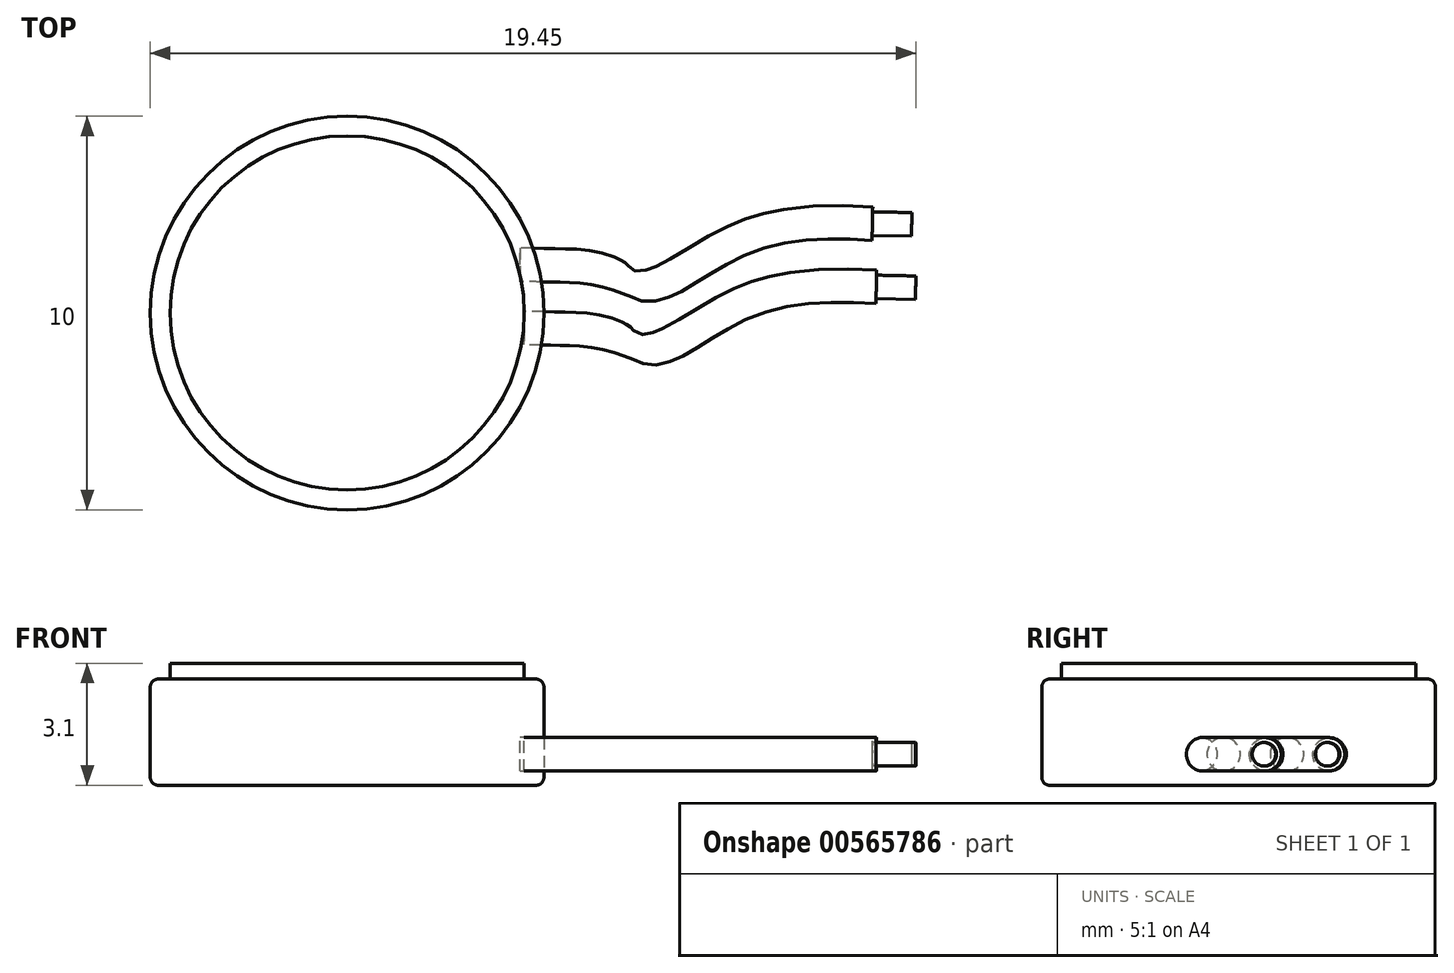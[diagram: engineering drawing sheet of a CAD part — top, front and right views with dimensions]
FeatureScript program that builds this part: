
annotation { "Feature Type Name" : "Feature", "Feature Type Description" : "" }
export const myFeature = defineFeature(function(context is Context, id is Id, definition is map)
    precondition{}
    {
        {
            var Q0;
            Q0=qCreatedBy(makeId("Top.planeOp"),FACE);
            var sketch = newSketch(context, id + "F0", { "sketchPlane" : qUnion([Q0])});
            skCircle(sketch, "E0", {"center": v(0, 0) * mm, "radius": 5 * mm});
            skSolve(sketch);
        }
        {
            var Q0;
            Q0=makeQuery(id+"F0.imprint","IMPRINT",FACE,{"disambiguationData":[TD([[makeQuery(id+"F0.imprint","IMPRINT",EDGE,{"derivedFrom":sQuery(id+"F0.wireOp",EDGE,"E0")}),1.0]])]});
            var Q1;
            Q1=sQuery(id+"F0.wireOp",EDGE,"E0");
            extrude(context, id + "F1", {"entities" : qUnion([Q0]), "surfaceEntities" : qUnion([Q1]), "depth" : 2.7 * mm, "offsetDistance" : 25 * mm});
        }
        {
            var Q0;
            Q0=makeQuery(id+"F1.opExtrude","CAP_FACE",FACE,{"disambiguationData":[OSD([sQuery(id+"F0.wireOp",EDGE,"E0")])],"isStart":false});
            var Q1;
            Q1=makeQuery(id+"F1.opExtrude","SWEPT_FACE",FACE,{"disambiguationData":[OSD([sQuery(id+"F0.wireOp",EDGE,"E0")])]});
            var Q2;
            Q2=makeQuery(id+"F1.opExtrude","CAP_FACE",FACE,{"disambiguationData":[OSD([sQuery(id+"F0.wireOp",EDGE,"E0")])],"isStart":true});
            fillet(context, id + "F2", {"entities" : qUnion([Q0, Q1, Q2]), "radius" : 0.2 * mm, "tangentPropagation" : true, "allowEdgeOverflow" : false});
        }
        {
            var Q0;
            Q0=makeQuery(id+"F1.opExtrude","CAP_FACE",FACE,{"disambiguationData":[OSD([sQuery(id+"F0.wireOp",EDGE,"E0")])],"isStart":false});
            var sketch = newSketch(context, id + "F3", { "sketchPlane" : qUnion([Q0])});
            skCircle(sketch, "E1", {"center": v(0, 0) * mm, "radius": 4.5 * mm});
            skSolve(sketch);
        }
        {
            var Q0;
            Q0=qCreatedBy(makeId("Right.planeOp"),FACE);
            var sketch = newSketch(context, id + "F4", { "sketchPlane" : qUnion([Q0])});
            skCircle(sketch, "E2", {"center": v(-5.9, -1.01) * mm, "radius": 0.53 * mm});
            skCircle(sketch, "E3.0", {"center": v(-5.9, -1.01) * mm, "radius": 0.43 * mm});
            skSolve(sketch);
        }
        {
            var Q0;
            Q0=qCreatedBy(makeId("Top.planeOp"),FACE);
            var sketch = newSketch(context, id + "F5", { "sketchPlane" : qUnion([Q0])});
            skFitSpline(sketch, "E4", {"points": [v(0.86, -7.42) * mm, v(2.15, -7.53) * mm, v(4.15, -7.61) * mm, v(6.53, -6.55) * mm, v(9.78, -6.4) * mm], "startDerivative": vector(6.34, -0.31) * mm, "endDerivative": vector(11.3, -0.8) * mm});
            skSolve(sketch);
        }
        {
            var Q0;
            Q0=makeQuery(id+"F4.imprint","IMPRINT",FACE,{"disambiguationData":[TD([[makeQuery(id+"F4.imprint","IMPRINT",EDGE,{"derivedFrom":sQuery(id+"F4.wireOp",EDGE,"E3.0")}),1.0]])]});
            var Q1;
            Q1=sQuery(id+"F5.wireOp",EDGE,"E4");
            sweep(context, id + "F6", {"profiles" : qUnion([Q0]), "path" : qUnion([Q1])});
        }
        {
            var Q0;
            Q0=makeQuery(id+"F6.opSweep","SWEPT_BODY",BODY,{"disambiguationData":[OSD([sQuery(id+"F4.wireOp",EDGE,"E3.0"),sQuery(id+"F5.wireOp",EDGE,"E4")])]});
            transform(context, id + "F7", {"entities" : qUnion([Q0]), "transformType" : TransformType.TRANSLATION_3D, "dx" : 5 * mm, "dy" : 6.12 * mm, "dz" : 1.6 * mm, "makeCopy" : false});
        }
        {
            var Q0;
            Q0=makeQuery(id+"F6.opSweep","SWEPT_BODY",BODY,{"disambiguationData":[OSD([sQuery(id+"F4.wireOp",EDGE,"E3.0"),sQuery(id+"F5.wireOp",EDGE,"E4")])]});
            transform(context, id + "F8", {"entities" : qUnion([Q0]), "transformType" : TransformType.TRANSLATION_3D, "dx" : 0 * mm, "dy" : 0 * mm, "dz" : 0.2 * mm, "makeCopy" : false});
        }
        {
            var Q0;
            Q0=makeQuery(id+"F6.opSweep","SWEPT_BODY",BODY,{"disambiguationData":[OSD([sQuery(id+"F4.wireOp",EDGE,"E3.0"),sQuery(id+"F5.wireOp",EDGE,"E4")])]});
            transform(context, id + "F9", {"entities" : qUnion([Q0]), "transformType" : TransformType.TRANSLATION_3D, "dx" : 0 * mm, "dy" : 1.3 * mm, "dz" : 0 * mm, "makeCopy" : true});
        }
        {
            var Q0;
            Q0=makeQuery(id+"F6.opSweep","SWEPT_BODY",BODY,{"disambiguationData":[OSD([sQuery(id+"F4.wireOp",EDGE,"E3.0"),sQuery(id+"F5.wireOp",EDGE,"E4")])]});
            transform(context, id + "F10", {"entities" : qUnion([Q0]), "transformType" : TransformType.TRANSLATION_3D, "dx" : -0.5 * mm, "dy" : -0.6 * mm, "dz" : 0 * mm, "makeCopy" : false});
        }
        {
            var Q0;
            Q0=makeQuery(id+"F9.opPattern","COPY",BODY,{"derivedFrom":makeQuery(id+"F6.opSweep","SWEPT_BODY",BODY,{"disambiguationData":[OSD([sQuery(id+"F4.wireOp",EDGE,"E3.0"),sQuery(id+"F5.wireOp",EDGE,"E4")])]}),"instanceName":"1"});
            transform(context, id + "F11", {"entities" : qUnion([Q0]), "transformType" : TransformType.TRANSLATION_3D, "dx" : -0.6 * mm, "dy" : -0.3 * mm, "dz" : 0 * mm, "makeCopy" : false});
        }
        {
            var Q0;
            Q0=makeQuery(id+"F3.imprint","IMPRINT",FACE,{"disambiguationData":[TD([[makeQuery(id+"F3.imprint","IMPRINT",EDGE,{"derivedFrom":sQuery(id+"F3.wireOp",EDGE,"E1")}),1.0]])]});
            var Q1;
            Q1=sQuery(id+"F3.wireOp",EDGE,"E1");
            extrude(context, id + "F12", {"entities" : qUnion([Q0]), "surfaceEntities" : qUnion([Q1]), "depth" : 0.4 * mm, "offsetDistance" : 25 * mm});
        }
        {
            var Q0;
            Q0=makeQuery(id+"F6.opSweep","CAP_FACE",FACE,{"disambiguationData":[OSD([sQuery(id+"F4.wireOp",EDGE,"E3.0"),sQuery(id+"F5.wireOp",VERTEX,"E4.end")])],"isStart":false});
            var sketch = newSketch(context, id + "F13", { "sketchPlane" : qUnion([Q0])});
            skCircle(sketch, "E5", {"center": v(0.94, 0.79) * mm, "radius": 0.3 * mm});
            skSolve(sketch);
        }
        {
            var Q0;
            Q0=makeQuery(id+"F9.opPattern","COPY",FACE,{"derivedFrom":makeQuery(id+"F6.opSweep","CAP_FACE",FACE,{"disambiguationData":[OSD([sQuery(id+"F4.wireOp",EDGE,"E3.0"),sQuery(id+"F5.wireOp",VERTEX,"E4.end")])],"isStart":false}),"instanceName":"1"});
            var sketch = newSketch(context, id + "F14", { "sketchPlane" : qUnion([Q0])});
            skCircle(sketch, "E6", {"center": v(2.55, 0.79) * mm, "radius": 0.3 * mm});
            skSolve(sketch);
        }
        {
            var Q0;
            Q0=makeQuery(id+"F13.imprint","IMPRINT",FACE,{"disambiguationData":[TD([[makeQuery(id+"F13.imprint","IMPRINT",EDGE,{"derivedFrom":sQuery(id+"F13.wireOp",EDGE,"E5")}),1.0]])]});
            var Q1;
            Q1=makeQuery(id+"F14.imprint","IMPRINT",FACE,{"disambiguationData":[TD([[makeQuery(id+"F14.imprint","IMPRINT",EDGE,{"derivedFrom":sQuery(id+"F14.wireOp",EDGE,"E6")}),1.0]])]});
            extrude(context, id + "F15", {"entities" : qUnion([Q0, Q1]), "depth" : 1 * mm, "offsetDistance" : 25 * mm});
        }
    });
